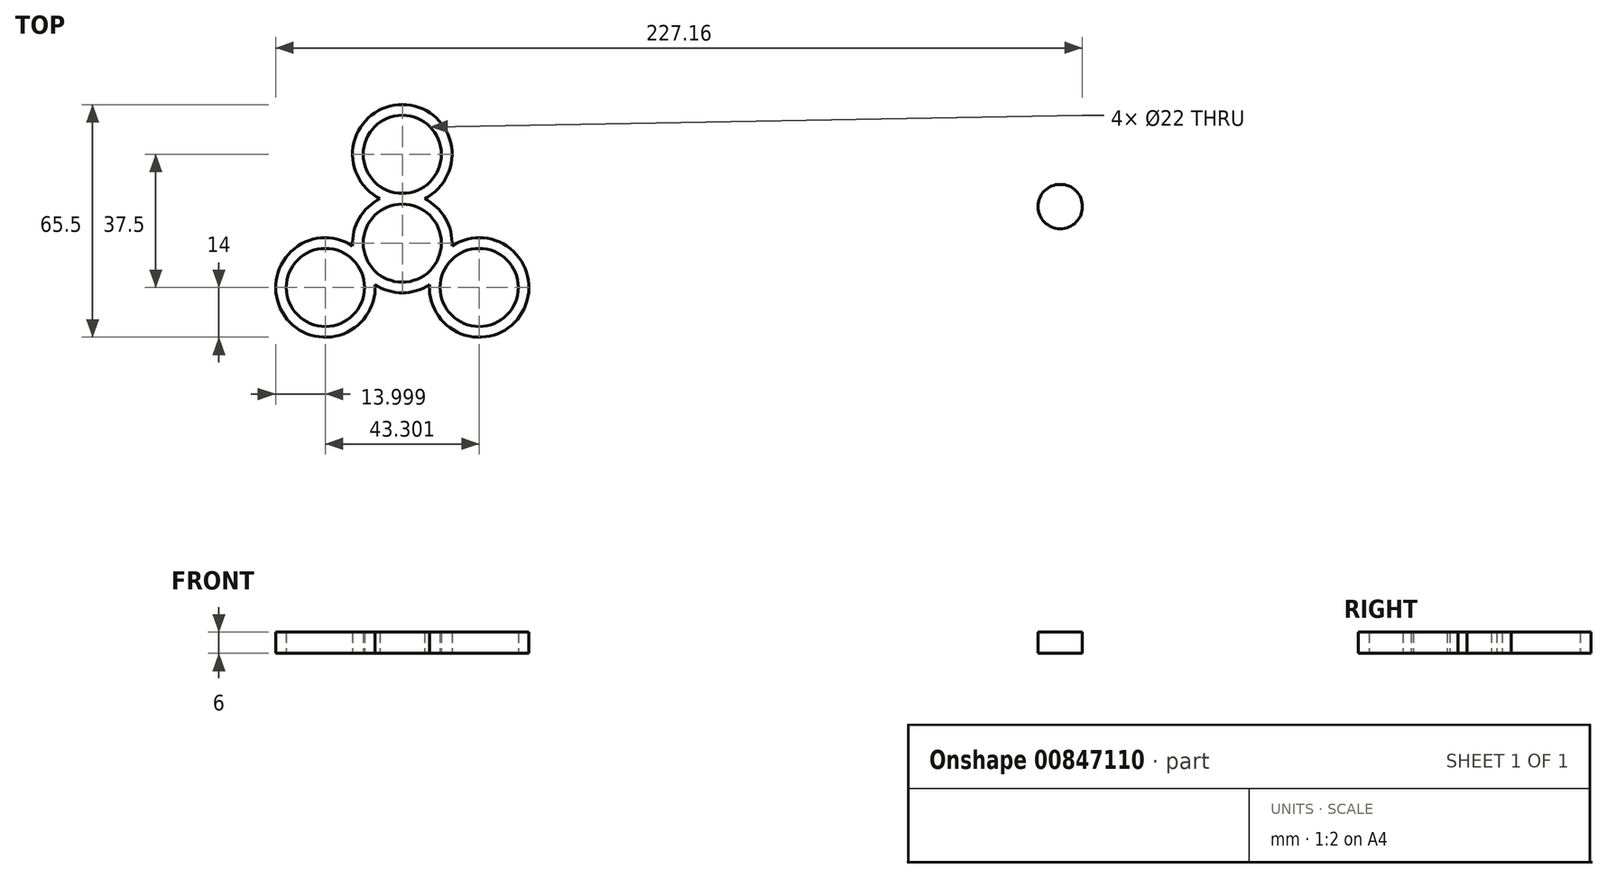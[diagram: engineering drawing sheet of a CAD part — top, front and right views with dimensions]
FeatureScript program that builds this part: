
annotation { "Feature Type Name" : "Feature", "Feature Type Description" : "" }
export const myFeature = defineFeature(function(context is Context, id is Id, definition is map)
    precondition{}
    {
        {
            var Q0;
            Q0=qCreatedBy(makeId("Top.planeOp"),FACE);
            var sketch = newSketch(context, id + "F0", { "sketchPlane" : qUnion([Q0])});
            skArc(sketch, "E0", {"start": v(9.53, 5.5) * mm, "mid": v(0, 11) * mm, "end": v(-9.53, 5.5) * mm});
            skCircle(sketch, "E1", {"center": v(0, 25) * mm, "radius": 11 * mm});
            skCircle(sketch, "E2", {"center": v(185.26, 10.29) * mm, "radius": 6.25 * mm});
            skArc(sketch, "E3", {"start": v(-6.3, 12.5) * mm, "mid": v(-9.62, 10.17) * mm, "end": v(-12.12, 7) * mm});
            skArc(sketch, "E4", {"start": v(6.3, 12.5) * mm, "mid": v(0, 39) * mm, "end": v(-6.3, 12.5) * mm});
            skArc(sketch, "E5.trimOffspring", {"start": v(12.12, 7) * mm, "mid": v(9.62, 10.17) * mm, "end": v(6.3, 12.5) * mm});
            skCircle(sketch, "E6.1.0", {"center": v(-21.65, -12.5) * mm, "radius": 11 * mm});
            skArc(sketch, "E6.1.1", {"start": v(-13.98, -0.79) * mm, "mid": v(-33.77, -19.5) * mm, "end": v(-7.67, -11.71) * mm});
            skArc(sketch, "E6.1.2", {"start": v(-9.53, 5.5) * mm, "mid": v(-9.53, -5.5) * mm, "end": v(0, -11) * mm});
            skArc(sketch, "E6.1.3", {"start": v(-7.67, -11.71) * mm, "mid": v(-4, -13.42) * mm, "end": v(0, -14) * mm});
            skArc(sketch, "E6.1.4", {"start": v(-12.12, 7) * mm, "mid": v(-13.62, 3.24) * mm, "end": v(-13.98, -0.79) * mm});
            skCircle(sketch, "E6.2.0", {"center": v(21.65, -12.5) * mm, "radius": 11 * mm});
            skArc(sketch, "E6.2.1", {"start": v(7.67, -11.71) * mm, "mid": v(33.77, -19.5) * mm, "end": v(13.98, -0.79) * mm});
            skArc(sketch, "E6.2.2", {"start": v(0, -11) * mm, "mid": v(9.53, -5.5) * mm, "end": v(9.53, 5.5) * mm});
            skArc(sketch, "E6.2.3", {"start": v(13.98, -0.79) * mm, "mid": v(13.62, 3.24) * mm, "end": v(12.12, 7) * mm});
            skArc(sketch, "E6.2.4", {"start": v(0, -14) * mm, "mid": v(4, -13.42) * mm, "end": v(7.67, -11.71) * mm});
            skSolve(sketch);
        }
        {
            var Q0;
            Q0 = qSketchRegion(id + "F0", true);
            extrude(context, id + "F1", {"entities" : qUnion([Q0]), "depth" : 6 * mm, "offsetDistance" : 25 * mm});
        }
    });
